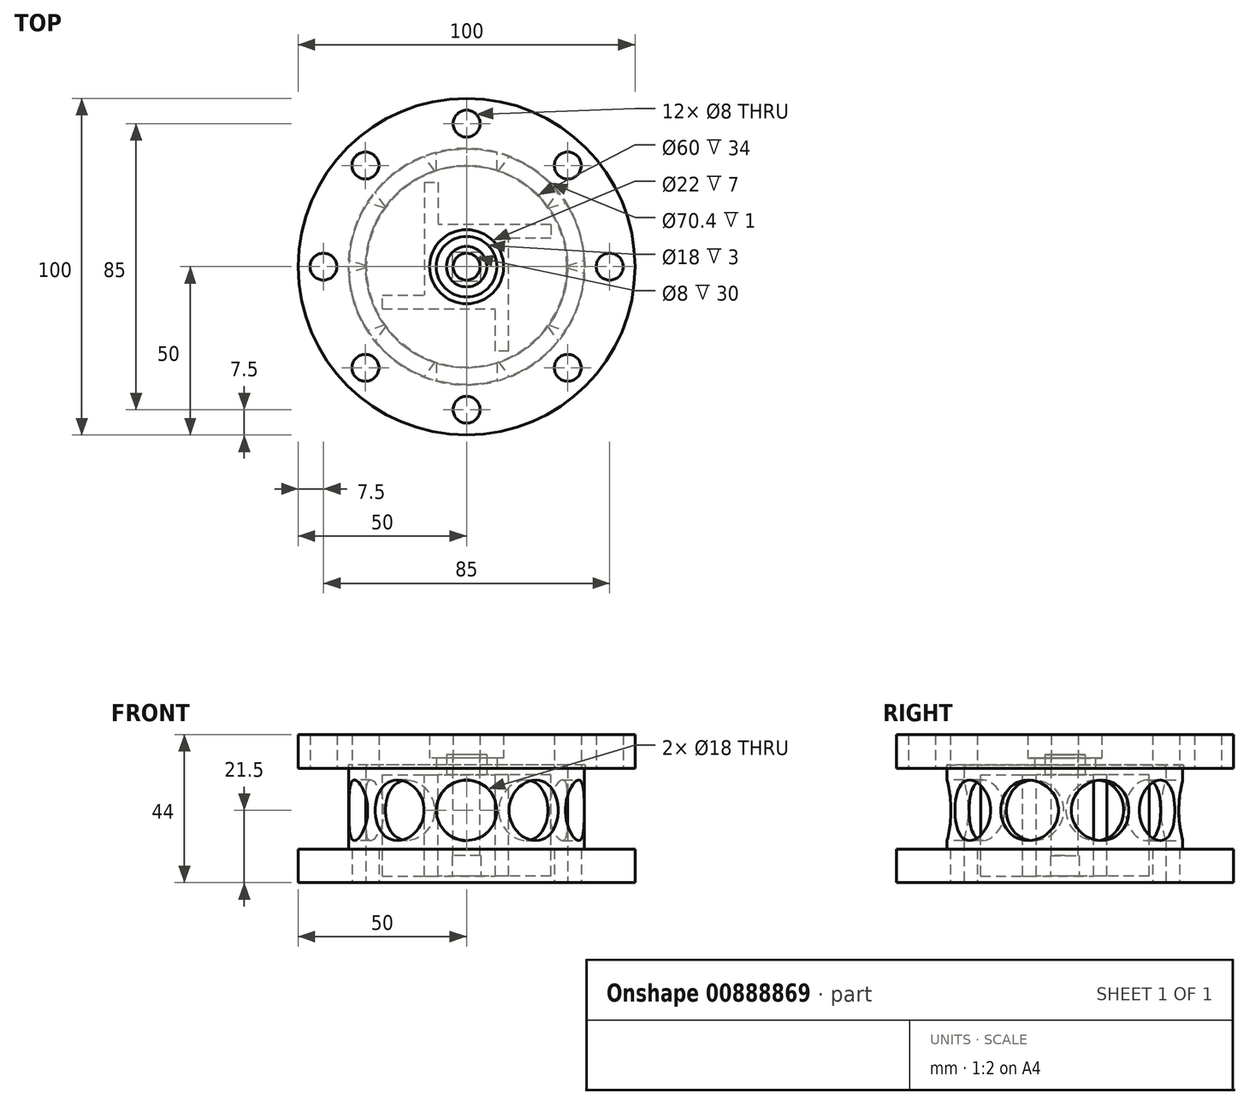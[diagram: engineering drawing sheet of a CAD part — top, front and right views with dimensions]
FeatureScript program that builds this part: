
annotation { "Feature Type Name" : "Feature", "Feature Type Description" : "" }
export const myFeature = defineFeature(function(context is Context, id is Id, definition is map)
    precondition{}
    {
        {
            var Q0;
            Q0=qCreatedBy(makeId("Top.planeOp"),FACE);
            cPlane(context, id + "F0", {"entities" : qUnion([Q0]), "cplaneType" : CPlaneType.OFFSET, "offset" : 34 * mm, "oppositeDirection" : true, "width" : 150 * mm, "height" : 150 * mm});
        }
        {
            var Q0;
            Q0=qCreatedBy(makeId("Top.planeOp"),FACE);
            cPlane(context, id + "F1", {"entities" : qUnion([Q0]), "cplaneType" : CPlaneType.OFFSET, "offset" : 2 * mm, "oppositeDirection" : true, "width" : 150 * mm, "height" : 150 * mm});
        }
        {
            var Q0;
            Q0=qCreatedBy(makeId("Front.planeOp"),FACE);
            cPlane(context, id + "F2", {"entities" : qUnion([Q0]), "cplaneType" : CPlaneType.OFFSET, "offset" : 35 * mm, "width" : 150 * mm, "height" : 150 * mm});
        }
        {
            var Q0;
            Q0=qCreatedBy(makeId("Top.planeOp"),FACE);
            var sketch = newSketch(context, id + "F3", { "sketchPlane" : qUnion([Q0])});
            skCircle(sketch, "E0", {"center": v(0, 0) * mm, "radius": 50 * mm});
            skCircle(sketch, "E1", {"center": v(0, 0) * mm, "radius": 42.5 * mm, "construction": true});
            skCircle(sketch, "E2", {"center": v(0, 42.5) * mm, "radius": 4 * mm});
            skCircle(sketch, "E3.1.1", {"center": v(-30.05, 30.05) * mm, "radius": 4 * mm});
            skCircle(sketch, "E3.2.1", {"center": v(-42.5, 0) * mm, "radius": 4 * mm});
            skCircle(sketch, "E3.3.1", {"center": v(-30.05, -30.05) * mm, "radius": 4 * mm});
            skCircle(sketch, "E3.4.1", {"center": v(0, -42.5) * mm, "radius": 4 * mm});
            skCircle(sketch, "E3.5.1", {"center": v(30.05, -30.05) * mm, "radius": 4 * mm});
            skCircle(sketch, "E3.6.1", {"center": v(42.5, 0) * mm, "radius": 4 * mm});
            skCircle(sketch, "E3.7.1", {"center": v(30.05, 30.05) * mm, "radius": 4 * mm});
            skCircle(sketch, "E4", {"center": v(0, 0) * mm, "radius": 11 * mm});
            skSolve(sketch);
        }
        {
            var Q0;
            Q0 = qSketchRegion(id + "F3", true);
            var Q1;
            Q1=makeQuery(id+"F3.imprint","IMPRINT",FACE,{"disambiguationData":[TD([[makeQuery(id+"F3.imprint","IMPRINT",EDGE,{"derivedFrom":sQuery(id+"F3.wireOp",EDGE,"E4")}),-1.0]])]});
            extrude(context, id + "F4", {"entities" : qUnion([Q0, Q1]), "depth" : 10 * mm, "offsetDistance" : 25 * mm});
        }
        {
            var Q0;
            Q0=qCreatedBy(id+"F0.planeOp",FACE);
            var sketch = newSketch(context, id + "F5", { "sketchPlane" : qUnion([Q0])});
            skCircle(sketch, "E5.0", {"center": v(0, 0) * mm, "radius": 50 * mm});
            skCircle(sketch, "E6.0", {"center": v(-30.05, 30.05) * mm, "radius": 4 * mm});
            skCircle(sketch, "E7.0", {"center": v(-30.05, -30.05) * mm, "radius": 4 * mm});
            skCircle(sketch, "E8.0", {"center": v(30.05, -30.05) * mm, "radius": 4 * mm});
            skCircle(sketch, "E9.0", {"center": v(30.05, 30.05) * mm, "radius": 4 * mm});
            skCircle(sketch, "E10", {"center": v(0, 0) * mm, "radius": 35 * mm});
            skCircle(sketch, "E11", {"center": v(0, 0) * mm, "radius": 30 * mm});
            skSolve(sketch);
        }
        {
            var Q0;
            Q0=makeQuery(id+"F5.imprint","IMPRINT",FACE,{"disambiguationData":[TD([[makeQuery(id+"F5.imprint","IMPRINT",EDGE,{"derivedFrom":sQuery(id+"F5.wireOp",EDGE,"E10")}),1.0]])]});
            extrude(context, id + "F6", {"entities" : qUnion([Q0]), "depth" : 35 * mm, "offsetDistance" : 25 * mm});
        }
        {
            var Q0;
            Q0 = qSketchRegion(id + "F5", true);
            extrude(context, id + "F7", {"entities" : qUnion([Q0]), "operationType" : NewBodyOperationType.ADD, "depth" : 10 * mm, "offsetDistance" : 25 * mm});
        }
        {
            var Q0;
            Q0=qCreatedBy(id+"F1.planeOp",FACE);
            var sketch = newSketch(context, id + "F8", { "sketchPlane" : qUnion([Q0])});
            skCircle(sketch, "E12.0", {"center": v(0, 0) * mm, "radius": 30 * mm, "construction": true});
            skCircle(sketch, "E13", {"center": v(0, 0) * mm, "radius": 4 * mm});
            skLineSegment(sketch, "E14", {"start": v(0, 42.18) * mm, "end": v(0, -43.72) * mm, "construction": true});
            skPoint(sketch, "E15.orphan", {"position": v(-3.74, 3.32) * mm});
            skPoint(sketch, "E16.orphan", {"position": v(-1.6, 3.67) * mm});
            skPoint(sketch, "E17.trimOffspring.end.orphan", {"position": v(1.6, 3.67) * mm});
            skPoint(sketch, "E18.orphan", {"position": v(3.74, 3.32) * mm});
            skPoint(sketch, "E19.orphan", {"position": v(4.31, -2.53) * mm});
            skPoint(sketch, "E20.orphan", {"position": v(-1.08, -4.88) * mm});
            skLineSegment(sketch, "E21", {"start": v(12.5, -25.05) * mm, "end": v(8.5, -25.05) * mm});
            skLineSegment(sketch, "E22", {"start": v(8.5, -25.05) * mm, "end": v(8.5, -12.5) * mm});
            skLineSegment(sketch, "E23.1.1", {"start": v(25.05, 8.5) * mm, "end": v(12.5, 8.5) * mm});
            skLineSegment(sketch, "E23.1.2", {"start": v(25.05, 12.5) * mm, "end": v(25.05, 8.5) * mm});
            skLineSegment(sketch, "E23.2.1", {"start": v(-8.5, 25.05) * mm, "end": v(-8.5, 12.5) * mm});
            skLineSegment(sketch, "E23.2.2", {"start": v(-12.5, 25.05) * mm, "end": v(-8.5, 25.05) * mm});
            skLineSegment(sketch, "E23.3.1", {"start": v(-25.05, -8.5) * mm, "end": v(-12.5, -8.5) * mm});
            skLineSegment(sketch, "E23.3.2", {"start": v(-25.05, -12.5) * mm, "end": v(-25.05, -8.5) * mm});
            skLineSegment(sketch, "E24", {"start": v(12.5, -25.05) * mm, "end": v(12.5, 8.5) * mm});
            skLineSegment(sketch, "E25", {"start": v(25.05, 12.5) * mm, "end": v(-8.5, 12.5) * mm});
            skLineSegment(sketch, "E26", {"start": v(-25.05, -12.5) * mm, "end": v(8.5, -12.5) * mm});
            skLineSegment(sketch, "E27", {"start": v(-12.5, 25.05) * mm, "end": v(-12.5, -8.5) * mm});
            skPoint(sketch, "E28.orphan", {"position": v(-9.17, -8.5) * mm});
            skPoint(sketch, "E29.orphan", {"position": v(-8.5, 9.17) * mm});
            skPoint(sketch, "E30.start.orphan", {"position": v(12.5, 0) * mm});
            skPoint(sketch, "E31.orphan", {"position": v(8.5, -9.17) * mm});
            skSolve(sketch);
        }
        {
            var Q0;
            Q0 = qSketchRegion(id + "F8", true);
            extrude(context, id + "F9", {"entities" : qUnion([Q0]), "oppositeDirection" : true, "depth" : 30 * mm, "offsetDistance" : 25 * mm});
        }
        {
            var Q0;
            Q0=qCreatedBy(id+"F2.planeOp",FACE);
            var sketch = newSketch(context, id + "F10", { "sketchPlane" : qUnion([Q0])});
            skLineSegment(sketch, "E32", {"start": v(-35, -25) * mm, "end": v(-35, 0) * mm, "construction": true});
            skLineSegment(sketch, "E33", {"start": v(35, 0) * mm, "end": v(35, -25) * mm, "construction": true});
            skLineSegment(sketch, "E34", {"start": v(-50, 0) * mm, "end": v(-50, 10) * mm, "construction": true});
            skLineSegment(sketch, "E35", {"start": v(50, 10) * mm, "end": v(50, 0) * mm, "construction": true});
            skLineSegment(sketch, "E36", {"start": v(-35, 0) * mm, "end": v(35, -25) * mm, "construction": true});
            skLineSegment(sketch, "E37", {"start": v(35, 0) * mm, "end": v(-35, -25) * mm, "construction": true});
            skCircle(sketch, "E38", {"center": v(0, -12.5) * mm, "radius": 9 * mm});
            skSolve(sketch);
        }
        {
            var Q0;
            Q0 = qSketchRegion(id + "F10", true);
            extrude(context, id + "F11", {"entities" : qUnion([Q0]), "oppositeDirection" : true, "depth" : 7 * mm, "offsetDistance" : 25 * mm});
        }
        {
            var Q0;
            Q0=makeQuery(id+"F11.opExtrude","SWEPT_BODY",BODY,{"disambiguationData":[OSD([sQuery(id+"F10.wireOp",EDGE,"E38")])]});
            var Q1;
            Q1=makeQuery(id+"F7.opExtrude","CAP_EDGE",EDGE,{"disambiguationData":[OSD([sQuery(id+"F5.wireOp",EDGE,"E5.0")])],"isStart":false});
            circularPattern(context, id + "F12", {"operationType" : NewBodyOperationType.REMOVE, "entities" : qUnion([Q0]), "axis" : qUnion([Q1]), "angle" : 360 * degree, "instanceCount" : 10, "equalSpace" : true});
        }
        {
            var Q0;
            Q0=qCreatedBy(makeId("Top.planeOp"),FACE);
            var sketch = newSketch(context, id + "F13", { "sketchPlane" : qUnion([Q0])});
            skCircle(sketch, "E39.0", {"center": v(0, 0) * mm, "radius": 30 * mm, "construction": true});
            skCircle(sketch, "E40.0", {"center": v(0, 0) * mm, "radius": 35 * mm, "construction": true});
            skCircle(sketch, "E41.0", {"center": v(0, 0) * mm, "radius": 35.2 * mm});
            skCircle(sketch, "E42.0", {"center": v(0, 0) * mm, "radius": 29.8 * mm});
            skSolve(sketch);
        }
        {
            var Q0;
            Q0 = qSketchRegion(id + "F13", true);
            extrude(context, id + "F14", {"entities" : qUnion([Q0]), "operationType" : NewBodyOperationType.REMOVE, "depth" : 1 * mm, "offsetDistance" : 25 * mm});
        }
        {
            var Q0;
            Q0=qCreatedBy(makeId("Top.planeOp"),FACE);
            var sketch = newSketch(context, id + "F15", { "sketchPlane" : qUnion([Q0])});
            skCircle(sketch, "E43.0", {"center": v(0, 0) * mm, "radius": 11 * mm});
            skCircle(sketch, "E44", {"center": v(0, 0) * mm, "radius": 9 * mm});
            skSolve(sketch);
        }
        {
            var Q0;
            Q0 = qSketchRegion(id + "F15", true);
            extrude(context, id + "F16", {"entities" : qUnion([Q0]), "operationType" : NewBodyOperationType.ADD, "depth" : 3 * mm, "offsetDistance" : 25 * mm});
        }
        {
            var Q0;
            Q0=makeQuery(id+"F9.opExtrude","CAP_FACE",FACE,{"disambiguationData":[OSD([sQuery(id+"F8.wireOp",EDGE,"E13"),sQuery(id+"F8.wireOp",EDGE,"E21"),sQuery(id+"F8.wireOp",EDGE,"E22"),sQuery(id+"F8.wireOp",EDGE,"E23.1.1"),sQuery(id+"F8.wireOp",EDGE,"E23.1.2"),sQuery(id+"F8.wireOp",EDGE,"E23.2.1"),sQuery(id+"F8.wireOp",EDGE,"E23.2.2"),sQuery(id+"F8.wireOp",EDGE,"E23.3.1"),sQuery(id+"F8.wireOp",EDGE,"E23.3.2"),sQuery(id+"F8.wireOp",EDGE,"E24"),sQuery(id+"F8.wireOp",EDGE,"E25"),sQuery(id+"F8.wireOp",EDGE,"E26"),sQuery(id+"F8.wireOp",EDGE,"E27")])],"isStart":false});
            var sketch = newSketch(context, id + "F17", { "sketchPlane" : qUnion([Q0])});
            skCircle(sketch, "E45.cCircle", {"center": v(0, 0) * mm, "radius": 4.25 * mm, "construction": true});
            skLineSegment(sketch, "E45.0", {"start": v(4.25, -4.25) * mm, "end": v(-4.25, -4.25) * mm});
            skLineSegment(sketch, "E45.1", {"start": v(-4.25, -4.25) * mm, "end": v(-4.25, 4.25) * mm});
            skLineSegment(sketch, "E45.2", {"start": v(-4.25, 4.25) * mm, "end": v(4.25, 4.25) * mm});
            skLineSegment(sketch, "E45.3", {"start": v(4.25, 4.25) * mm, "end": v(4.25, -4.25) * mm});
            skPoint(sketch, "E45.0.midPoint", {"position": v(0, -4.25) * mm});
            skSolve(sketch);
        }
        {
            var Q0;
            Q0 = qSketchRegion(id + "F17", true);
            extrude(context, id + "F18", {"entities" : qUnion([Q0]), "operationType" : NewBodyOperationType.REMOVE, "oppositeDirection" : true, "depth" : 6 * mm, "offsetDistance" : 25 * mm});
        }
        {
            var Q0;
            Q0=makeQuery(id+"F9.opExtrude","CAP_FACE",FACE,{"disambiguationData":[OSD([sQuery(id+"F8.wireOp",EDGE,"E13"),sQuery(id+"F8.wireOp",EDGE,"E21"),sQuery(id+"F8.wireOp",EDGE,"E22"),sQuery(id+"F8.wireOp",EDGE,"E23.1.1"),sQuery(id+"F8.wireOp",EDGE,"E23.1.2"),sQuery(id+"F8.wireOp",EDGE,"E23.2.1"),sQuery(id+"F8.wireOp",EDGE,"E23.2.2"),sQuery(id+"F8.wireOp",EDGE,"E23.3.1"),sQuery(id+"F8.wireOp",EDGE,"E23.3.2"),sQuery(id+"F8.wireOp",EDGE,"E24"),sQuery(id+"F8.wireOp",EDGE,"E25"),sQuery(id+"F8.wireOp",EDGE,"E26"),sQuery(id+"F8.wireOp",EDGE,"E27")])],"isStart":true});
            var sketch = newSketch(context, id + "F19", { "sketchPlane" : qUnion([Q0])});
            skCircle(sketch, "E46", {"center": v(0, 0) * mm, "radius": 6 * mm});
            skCircle(sketch, "E47.0", {"center": v(0, 0) * mm, "radius": 4 * mm});
            skSolve(sketch);
        }
        {
            var Q0;
            Q0 = qSketchRegion(id + "F19", true);
            extrude(context, id + "F20", {"entities" : qUnion([Q0]), "operationType" : NewBodyOperationType.ADD, "depth" : 6 * mm, "offsetDistance" : 25 * mm});
        }
    });
